# Revit family: Sanitary_Mirrors_Sloan-Valve_MLs
name_source: partatom
category: Furniture
units: mm (PartAtom-declared; Revit-internal decimal feet)

## family parameters
Cut with Voids When Loaded = No
Host = Face
OmniClass Number = 23.40.95.17.17
OmniClass Title = Mirrors
Room Calculation Point = No
Shared = No

## types (5) — shared parameters
Apparent Load = 550 VA
Current = 5 A
Custom Size Note = Please reach out to Sloan Valve Company for information on custom sizes.
Default Elevation = 4' - 0"
Depth = 0' - 2"
Frequency = 60 Hz
Height = 3' - 0"
Manufacturer = Sloan Valve
Number of Poles = 1
Power Factor = 0.8
Product Material = Sloan Valve - Finish - Polished Chrome
Product data url = https://bimobject.com
Real Height = 3' - 0"
Real Width = 2' - 0"
URL = www.sloanvalve.com
Version = 1
Voltage = 110 V
Weight = 32.00 lbf
Width = 2' - 0"
z_Case Back Height = 2' - 9 1/2"
z_Case Back Width = 1' - 9 1/2"
z_Case Back Width Side = 0' - 2"
z_Case Back Width Top = 0' - 4"
z_Cutout Height = 0' - 5"
z_Cutout Width = 0' - 3"
z_Left Offset = 0' - 1"
z_Top Offset = 0' - 1"

## per-type parameters (varying)
| type | 2 Edge | 2 Inset | 4 Edge | 4 Inset | Back Lit | Case Back | Description | Part Number | z_Connector Side Offset | z_Connector Top Offset |
| ML 2 Edge-24x36-6000K | Yes | No | No | No | No | Yes | 24" x 36", Sloan Wall-hung Hardwired 2 Edge LED Mirror. | 32920003 | 1' - 0" | 1' - 8 1/2" |
| ML 2 Inset-24x36-6000K | No | Yes | No | No | No | Yes | 24" x 36", Sloan Wall-hung Hardwired 2 Inset LED Mirror. | 32920001 | 1' - 0" | 1' - 8 1/2" |
| ML 4 Edge-24x36-6000K | No | No | Yes | No | No | Yes | 24" x 36", Sloan Wall-hung Hardwired 4 Edge LED Mirror. | 32920004 | 1' - 0" | 1' - 8 1/2" |
| ML 4 Inset-24x36-6000K | No | No | No | Yes | No | Yes | 24" x 36", Sloan Wall-hung Hardwired 4 Inset LED Mirror. | 32920002 | 1' - 0" | 1' - 8 1/2" |
| ML Back Lit-24x36-6000K | No | No | No | No | Yes | No | 24" x 36", Sloan Wall-hung Hardwired Back Lit LED Mirror. | 32920005 | 0' - 5" | 2' - 7" |

note: column(s) folded — value = type name in every type: Model

## geometry (parser evidence)
native form markers: Sweep x6
no freeform markers — native parametric forms only
